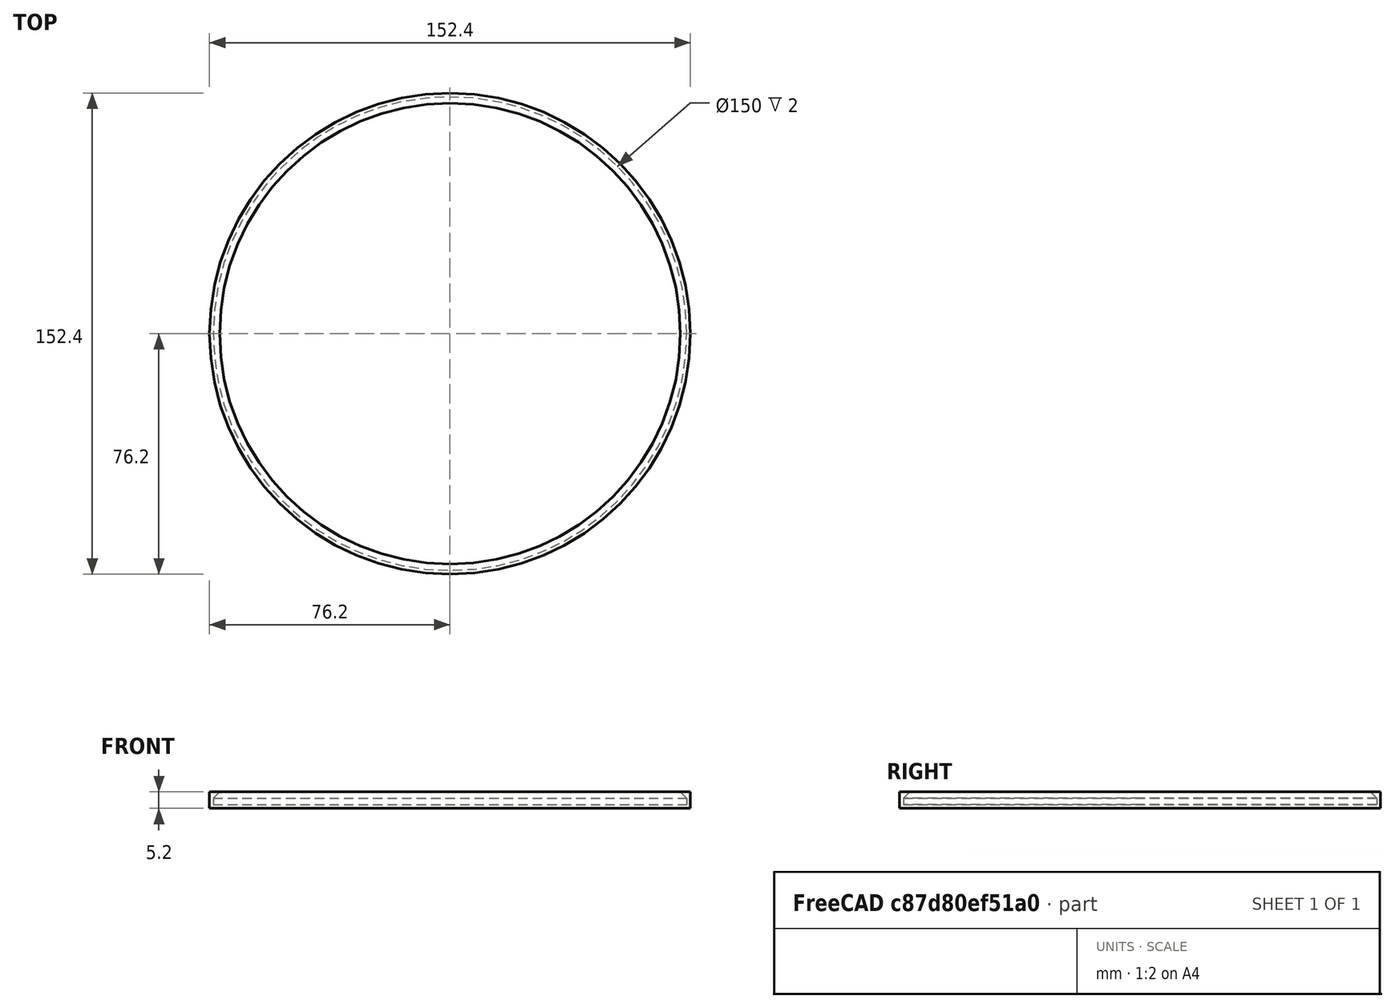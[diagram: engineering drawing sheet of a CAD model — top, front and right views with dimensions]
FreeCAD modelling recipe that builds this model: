
FCSTD DOCUMENT  (FreeCAD 1.0R39109 (Git))
Label: can_cover
License: All rights reserved
LicenseURL: http://en.wikipedia.org/wiki/All_rights_reserved
objects: Spreadsheet::Sheet×2, Sketcher::SketchObject×1, PartDesign::Revolution×1, PartDesign::Body×1
note: 6 computed .brp shape members not serialized (recipe doc carries the construction recipe); baked Part::Feature solids carry a one-line shape summary decoded from their .brp

FEATURE [Spreadsheet::Sheet] Spreadsheet  label="settings"
  cells = A1='Inner diameter; B1(dia_inner)=150; A2='wall thickness; B2(thick_wall)=1.2; A3='lip thickness; B3(thick_lip)=2; A4='edge height; B4(height_edge)=4
FEATURE [Sketcher::SketchObject] Sketch
  ArcFitTolerance = 0
  AttachmentSupport = -> [XZ_Plane]
  FullyConstrained = true
  MakeInternals = false
  MapMode = 5
  Placement = pos=(0,0,0) rot=(1,0,0;1.5708rad)
  expr: Constraints[22] = <<settings>>.thick_lip
  expr: Constraints[24] = <<settings>>.dia_inner / 2
  expr: Constraints[25] = <<settings>>.thick_wall
  expr: Constraints[6] = <<settings>>.thick_wall
  expr: Constraints[9] = <<settings>>.height_edge
  sketch-geometry (9):
    g0: LineSegment StartX=0 StartY=1.2 StartZ=0 EndX=0 EndY=0 EndZ=0
    g1: LineSegment StartX=0 StartY=1.2 StartZ=0 EndX=-75 EndY=1.2 EndZ=0
    g2: LineSegment [constr] StartX=0 StartY=1.2 StartZ=0 EndX=-76.2 EndY=1.2 EndZ=0
    g3: LineSegment [constr] StartX=-75 StartY=1.2 StartZ=0 EndX=-75 EndY=5.2 EndZ=0
    g4: LineSegment StartX=-76.2 StartY=5.2 StartZ=0 EndX=-76.2 EndY=0 EndZ=0
    g5: LineSegment StartX=0 StartY=0 StartZ=0 EndX=-76.2 EndY=0 EndZ=0
    g6: LineSegment StartX=-76.2 StartY=5.2 StartZ=0 EndX=-73 EndY=5.2 EndZ=0
    g7: LineSegment StartX=-73 StartY=5.2 StartZ=0 EndX=-75 EndY=3.2 EndZ=0
    g8: LineSegment StartX=-75 StartY=3.2 StartZ=0 EndX=-75 EndY=1.2 EndZ=0
  constraints (26):
    c: PointOnObject(g0,g-2)
    c: Coincident(g0,g-1)
    c: Coincident(g1,g0)
    c: Horizontal(g1)
    c: Coincident(g2,g0)
    c: PointOnObject(g2,g1)
    c: Distance(g2,g1) = 1.2
    c: Coincident(g3,g1)
    c: Vertical(g3)
    c: Distance(g3) = 4
    c: PointOnObject(g2,g4)
    c: Coincident(g5,g0)
    c: PointOnObject(g5,g-1)
    c: Vertical(g5,g2)
    c: Coincident(g4,g5)
    c: Horizontal(g4,g3)
    c: Coincident(g6,g4)
    c: Coincident(g7,g6)
    c: PointOnObject(g7,g3)
    c: Coincident(g8,g7)
    c: Coincident(g8,g1)
    c: PointOnObject(g3,g6)
    c: Distance(g3,g6) = 2
    c: Angle(g6,g7) = 0.785398
    c: Distance(g1,g0) = 75
    c: Distance(g0,g0) = 1.2
FEATURE [PartDesign::Revolution] Revolution  label="main_revolution"
  Angle = 360
  Angle2 = 60
  Axis = (0,2e-16,1)
  Base = (0,0,0)
  Placement = pos=(0,0,0) rot=(1,0,0;1.5708rad)
  Profile = -> Sketch
  ReferenceAxis = -> Sketch [V_Axis]
  Suppressed = false
  Type = 0
FEATURE [PartDesign::Body] Body  label="can cover"
  AllowCompound = false
  Group = -> [Sketch,Revolution]
  Origin = -> Origin
  Tip = -> Revolution
FEATURE [Spreadsheet::Sheet] Spreadsheet001  label="example settings"
  cells = A1='Object; B1='Inner diameter; C1='wall thickness; D1='lip thickness; E1='edge height; A2='Big can of catfood; B2=102; C2=1.2; D2=1; E2=5; A3='Skyr arla; B3=96; C3=1.2; D3=1; E3=3; A4='Ikea glass small bowl; B4=150; C4=1.2; D4=2; E4=4
